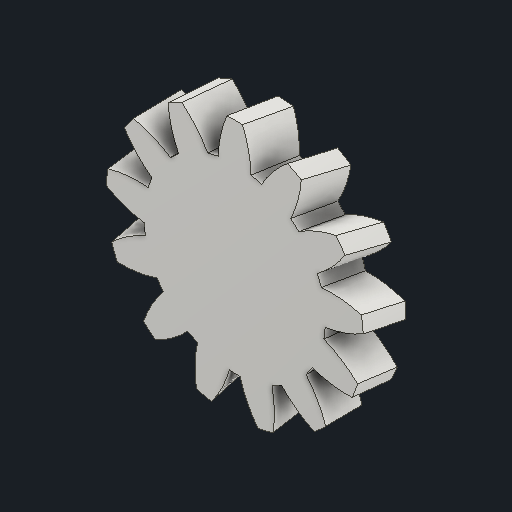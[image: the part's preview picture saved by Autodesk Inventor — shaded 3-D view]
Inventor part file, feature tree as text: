
AUTODESK INVENTOR PART (.ipt)
format: ipt  version: 2024.2 (Build 282272000, 272)  size: 353,280 bytes
history: native  units: in
note: dims shown in document units (in); Inventor stores cm internally (conversion verified against a paired STEP export)
features: other x12, plane x3, sketch x2
ambient origin geometry x8: Origin, YZ Plane, XZ Plane, XY Plane, X Axis, Y Axis, Z Axis, Center Point
bodies: Solid1 (feature_tree)
feature tree (17):
  other  "Spur Gear1"
  other  "Solid1::Spur Gear1"
  other  "TaggingFeature1"
  sketch  "Sketch1"  dims[d0=0.3937in]
  sketch  "Sketch2"  dims[d9=0.0in d14=0.0in d15=1.3982in d16=0.0in d17=0.0in d18=0.0in d19=1.3982in]
  plane  "XZ Plane_1"
  plane  "Work Plane2"
  plane  "Work Plane3"
  other  "Srf1"
  other  "Srf1::Derived"
  other  "Start plane iMate"
  other  "Distance iMate"
  other  "Position iMate"
  other  "Mesh iMate"
  other  "Axis iMate"
  other  "Mesh iMate2"
  other  "Align iMate"
